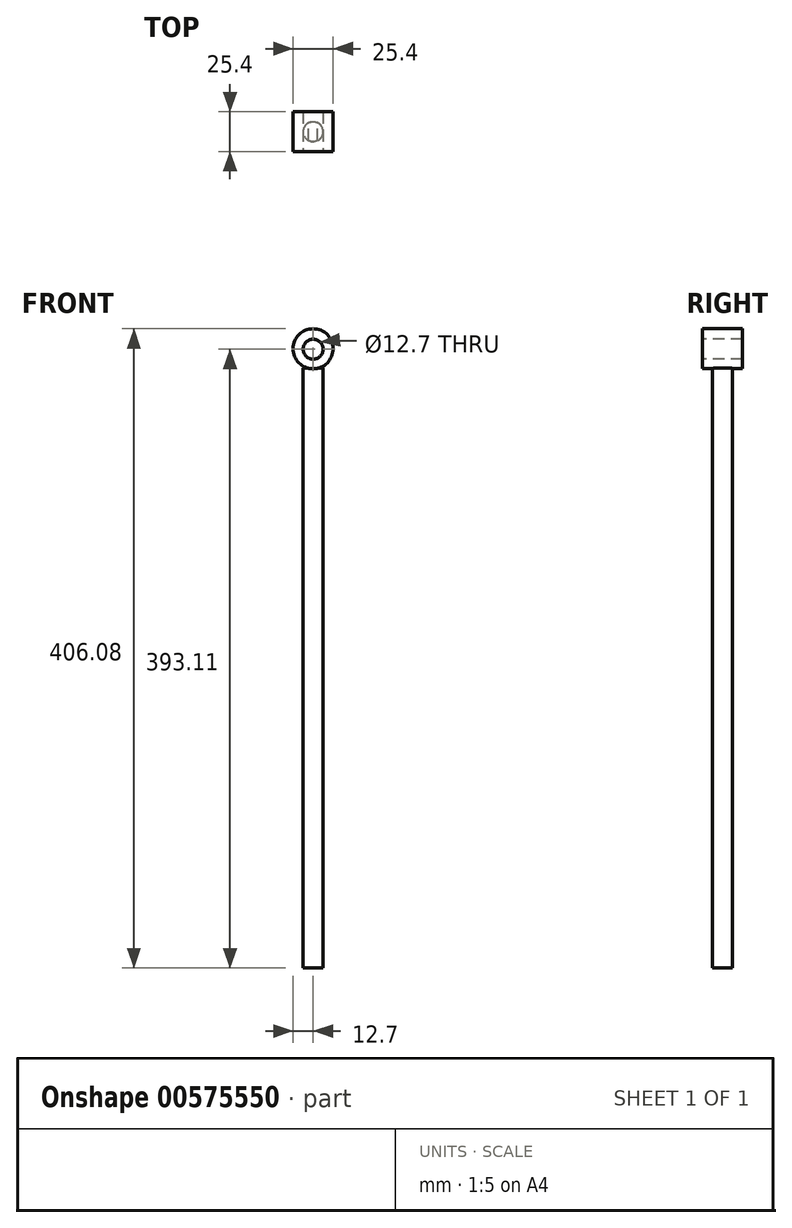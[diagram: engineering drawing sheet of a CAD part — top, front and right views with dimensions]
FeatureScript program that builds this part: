
annotation { "Feature Type Name" : "Feature", "Feature Type Description" : "" }
export const myFeature = defineFeature(function(context is Context, id is Id, definition is map)
    precondition{}
    {
        {
            var Q0;
            Q0=qCreatedBy(makeId("Top.planeOp"),FACE);
            var sketch = newSketch(context, id + "F0", { "sketchPlane" : qUnion([Q0])});
            skCircle(sketch, "E0", {"center": v(0, 0) * mm, "radius": 6.35 * mm});
            skSolve(sketch);
        }
        {
            var Q0;
            Q0=makeQuery(id+"F0.imprint","IMPRINT",FACE,{"disambiguationData":[TD([[makeQuery(id+"F0.imprint","IMPRINT",EDGE,{"derivedFrom":sQuery(id+"F0.wireOp",EDGE,"E0")}),1.0]])]});
            extrude(context, id + "F1", {"entities" : qUnion([Q0]), "depth" : -381 * mm, "offsetDistance" : 25.4 * mm});
        }
        {
            var Q0;
            Q0=qCreatedBy(makeId("Front.planeOp"),FACE);
            var sketch = newSketch(context, id + "F2", { "sketchPlane" : qUnion([Q0])});
            skCircle(sketch, "E1", {"center": v(0, 12.38) * mm, "radius": 12.7 * mm});
            skSolve(sketch);
        }
        {
            var Q0;
            Q0=makeQuery(id+"F2.imprint","IMPRINT",FACE,{"disambiguationData":[TD([[makeQuery(id+"F2.imprint","IMPRINT",EDGE,{"derivedFrom":sQuery(id+"F2.wireOp",EDGE,"E1")}),1.0]])]});
            extrude(context, id + "F3", {"entities" : qUnion([Q0]), "operationType" : NewBodyOperationType.ADD, "endBound" : BoundingType.SYMMETRIC, "depth" : 25.4 * mm, "offsetDistance" : 25.4 * mm});
        }
        {
            var Q0;
            Q0=qCreatedBy(makeId("Front.planeOp"),FACE);
            var sketch = newSketch(context, id + "F4", { "sketchPlane" : qUnion([Q0])});
            skCircle(sketch, "E2", {"center": v(0, 12.11) * mm, "radius": 6.35 * mm});
            skSolve(sketch);
        }
        {
            var Q0;
            Q0=qSketchRegion(id+"F4",true);
            extrude(context, id + "F5", {"entities" : qUnion([Q0]), "operationType" : NewBodyOperationType.REMOVE, "endBound" : BoundingType.SYMMETRIC, "oppositeDirection" : true, "depth" : 25.4 * mm, "offsetDistance" : 25.4 * mm});
        }
    });
